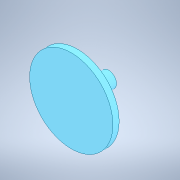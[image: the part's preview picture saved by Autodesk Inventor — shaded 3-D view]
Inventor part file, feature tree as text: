
AUTODESK INVENTOR PART (.ipt)
format: ipt  version: 2020.1 (Build 241239000, 239)  size: 237,056 bytes
history: native  units: in
note: dims shown in document units (in); Inventor stores cm internally (conversion verified against a paired STEP export)
features: extrude x5, sketch x5, projected_geometry x3, plane x2, split x1
ambient origin geometry x8: Origin, YZ Plane, XZ Plane, XY Plane, X Axis, Y Axis, Z Axis, Center Point
bodies: Solid1 (feature_tree)
feature tree (16):
  extrude  "Extrusion1"  Depth=0.0787in
  extrude  "Extrusion2"  Depth=0.1969in
  plane  "Work Plane1"
  extrude  "Extrusion7"  TaperAngle=0.0deg  [1 undecoded]
  extrude  "Extrusion8"  Depth=0.0394in
  extrude  "Extrusion10"  TaperAngle=0.0deg  [1 undecoded]
  plane  "Work Plane3"
  split  "Split1"
  sketch  "Sketch1"  dims[d0=1.0499in d1=0.0787in]
  sketch  "Sketch2"  dims[d2=0.0in d3=0.1969in]
  sketch  "Sketch5"  dims[d4=0.2756in d5=0.0in]
  projected_geometry  "Projected Loop2"
  sketch  "Sketch6"  dims[d17=-0.0787in d18=0.0394in]
  projected_geometry  "Projected Loop4"
  sketch  "Sketch8"  dims[d19=0.0394in d20=0.0in d23=0.1969in d24=0.1969in d25=0.9706in d27=0.0984in d28=0.0in d32=0.1181in d33=0.0in d34=0.0in]
  projected_geometry  "Projected Loop5"
note: 2 required parameter values undecoded (feature->parameter linkage not recoverable at this tier; creation-order binding heuristic only, values carry confidence <= 0.55)
